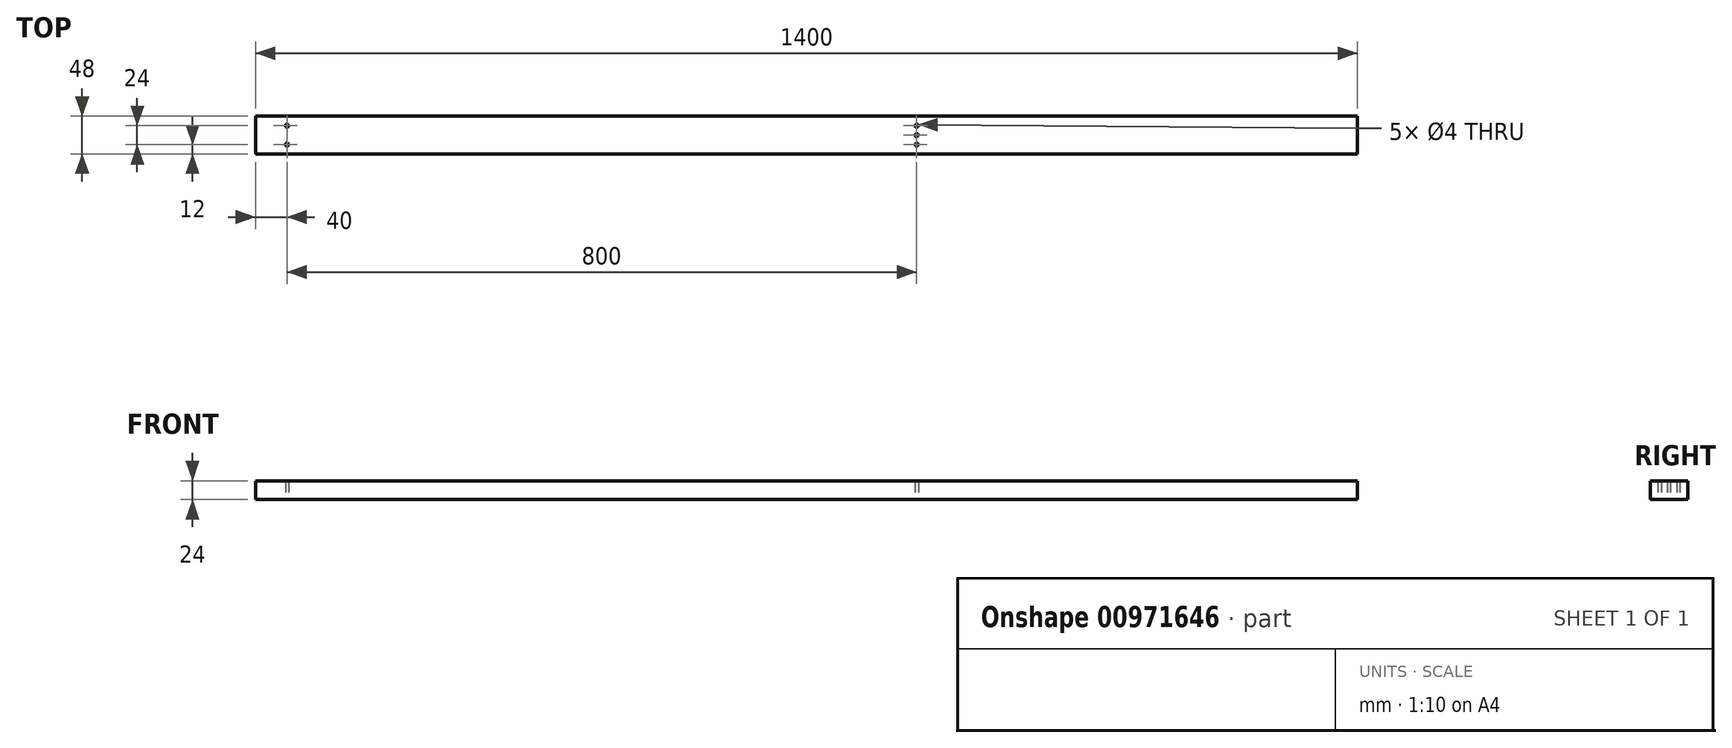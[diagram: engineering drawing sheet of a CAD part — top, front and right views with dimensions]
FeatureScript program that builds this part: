
annotation { "Feature Type Name" : "Feature", "Feature Type Description" : "" }
export const myFeature = defineFeature(function(context is Context, id is Id, definition is map)
    precondition{}
    {
        {
            var Q0;
            Q0=qCreatedBy(makeId("Top.planeOp"),FACE);
            var sketch = newSketch(context, id + "F0", { "sketchPlane" : qUnion([Q0])});
            skLineSegment(sketch, "E0.bottom", {"start": v(700, -24) * mm, "end": v(-700, -24) * mm});
            skLineSegment(sketch, "E0.top", {"start": v(700, 24) * mm, "end": v(-700, 24) * mm});
            skLineSegment(sketch, "E0.left", {"start": v(700, -24) * mm, "end": v(700, 24) * mm});
            skLineSegment(sketch, "E0.right", {"start": v(-700, -24) * mm, "end": v(-700, 24) * mm});
            skPoint(sketch, "E0.middle", {"position": v(0, 0) * mm});
            skLineSegment(sketch, "E1", {"start": v(-700, 0) * mm, "end": v(-660, 0) * mm});
            skLineSegment(sketch, "E2", {"start": v(-660, 0) * mm, "end": v(-660, 12) * mm});
            skLineSegment(sketch, "E3", {"start": v(-660, 0) * mm, "end": v(-660, -12) * mm});
            skCircle(sketch, "E4", {"center": v(-660, 12) * mm, "radius": 2 * mm});
            skCircle(sketch, "E5", {"center": v(-660, -12) * mm, "radius": 2 * mm});
            skLineSegment(sketch, "E6", {"start": v(-660, 0) * mm, "end": v(140, 0) * mm});
            skLineSegment(sketch, "E7", {"start": v(140, 0) * mm, "end": v(140, 12) * mm});
            skLineSegment(sketch, "E8", {"start": v(140, 0) * mm, "end": v(140, -12) * mm});
            skCircle(sketch, "E9", {"center": v(140, -12) * mm, "radius": 2 * mm});
            skCircle(sketch, "E10", {"center": v(140, 12) * mm, "radius": 2 * mm});
            skCircle(sketch, "E11", {"center": v(140, 0) * mm, "radius": 2 * mm});
            skSolve(sketch);
        }
        {
            var Q0;
            {var subQ3=sQuery(id+"F0.wireOp",EDGE,"E0.bottom");Q0=makeQuery(id+"F0.imprint","IMPRINT",FACE,{"disambiguationData":[TD([[makeQuery(id+"F0.imprint","IMPRINT",EDGE,{"derivedFrom":subQ3}),-1.0]])]});}
            extrude(context, id + "F1", {"entities" : qUnion([Q0]), "depth" : 24 * mm, "offsetDistance" : 25 * mm});
        }
    });
